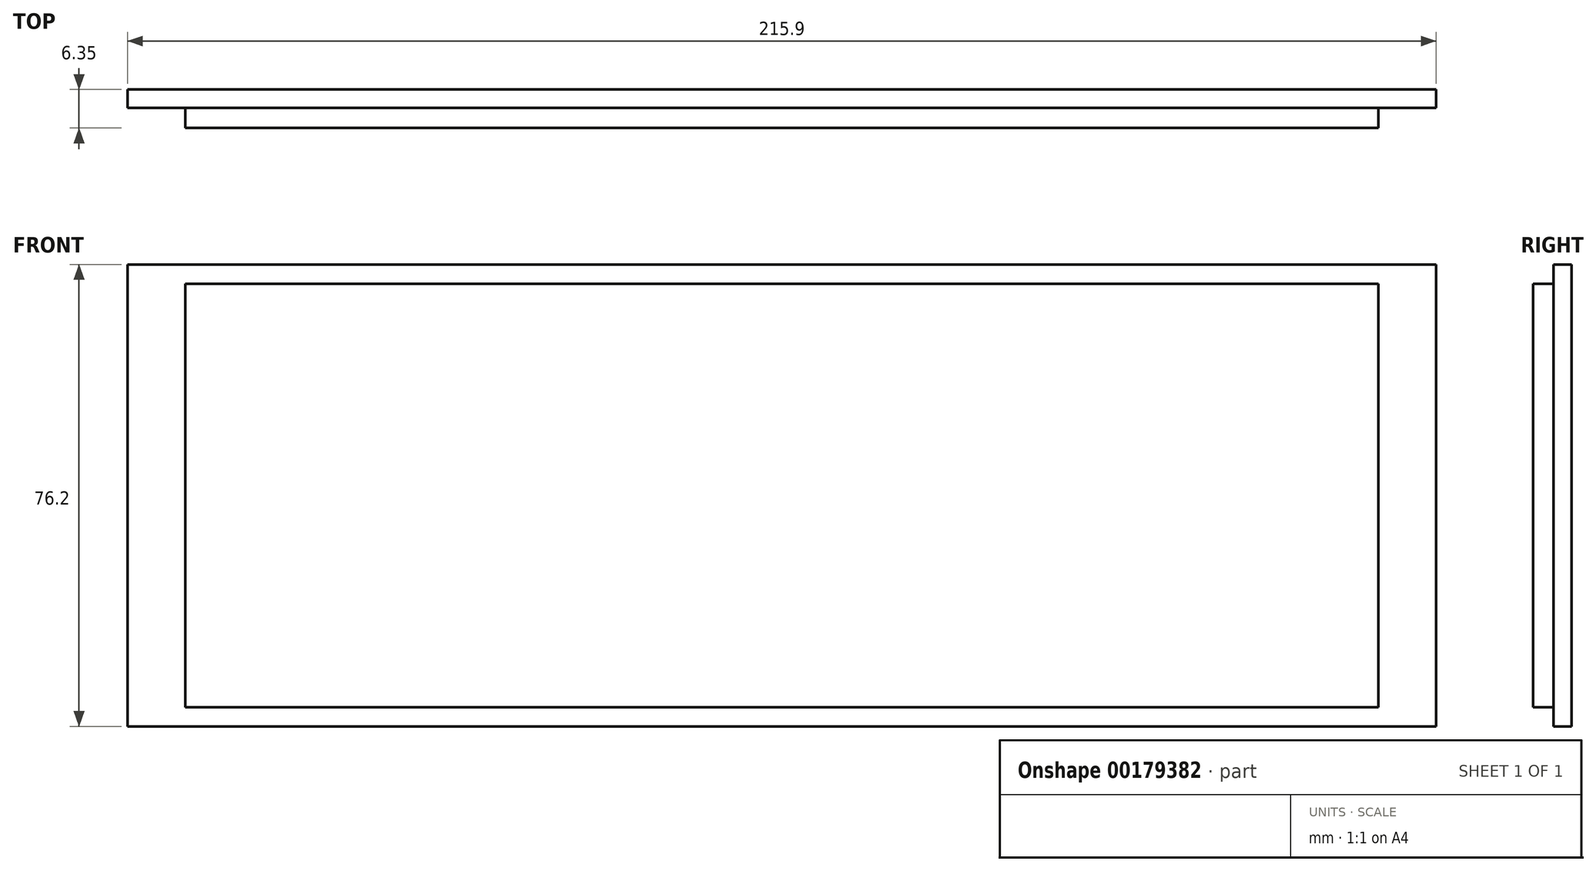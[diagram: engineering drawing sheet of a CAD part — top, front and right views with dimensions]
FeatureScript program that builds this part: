
annotation { "Feature Type Name" : "Feature", "Feature Type Description" : "" }
export const myFeature = defineFeature(function(context is Context, id is Id, definition is map)
    precondition{}
    {
        {
            var Q0;
            Q0=qCreatedBy(makeId("Front.planeOp"),FACE);
            var sketch = newSketch(context, id + "F0", { "sketchPlane" : qUnion([Q0])});
            skLineSegment(sketch, "E0.bottom", {"start": v(-117.56, 40.25) * mm, "end": v(98.34, 40.25) * mm});
            skLineSegment(sketch, "E0.top", {"start": v(-117.56, -35.95) * mm, "end": v(98.34, -35.95) * mm});
            skLineSegment(sketch, "E0.left", {"start": v(-117.56, 40.25) * mm, "end": v(-117.56, -35.95) * mm});
            skLineSegment(sketch, "E0.right", {"start": v(98.34, 40.25) * mm, "end": v(98.34, -35.95) * mm});
            skSolve(sketch);
        }
        {
            var Q0;
            Q0=makeQuery(id+"F0.imprint","IMPRINT",FACE,{"disambiguationData":[TD([[makeQuery(id+"F0.imprint","IMPRINT",EDGE,{"derivedFrom":sQuery(id+"F0.wireOp",EDGE,"E0.bottom")}),-1.0]])]});
            var sketch = newSketch(context, id + "F1", { "sketchPlane" : qUnion([Q0])});
            skLineSegment(sketch, "E1.bottom", {"start": v(-108.04, 37.08) * mm, "end": v(88.81, 37.08) * mm});
            skLineSegment(sketch, "E1.top", {"start": v(-108.04, -32.77) * mm, "end": v(88.81, -32.77) * mm});
            skLineSegment(sketch, "E1.left", {"start": v(-108.04, 37.08) * mm, "end": v(-108.04, -32.77) * mm});
            skLineSegment(sketch, "E1.right", {"start": v(88.81, 37.08) * mm, "end": v(88.81, -32.77) * mm});
            skSolve(sketch);
        }
        {
            var Q0;
            Q0 = qSketchRegion(id + "F0", true);
            extrude(context, id + "F2", {"entities" : qUnion([Q0]), "depth" : 3 * mm});
        }
        {
            var Q0;
            Q0 = qSketchRegion(id + "F1", true);
            extrude(context, id + "F3", {"entities" : qUnion([Q0]), "operationType" : NewBodyOperationType.ADD, "depth" : 6.35 * mm});
        }
    });
